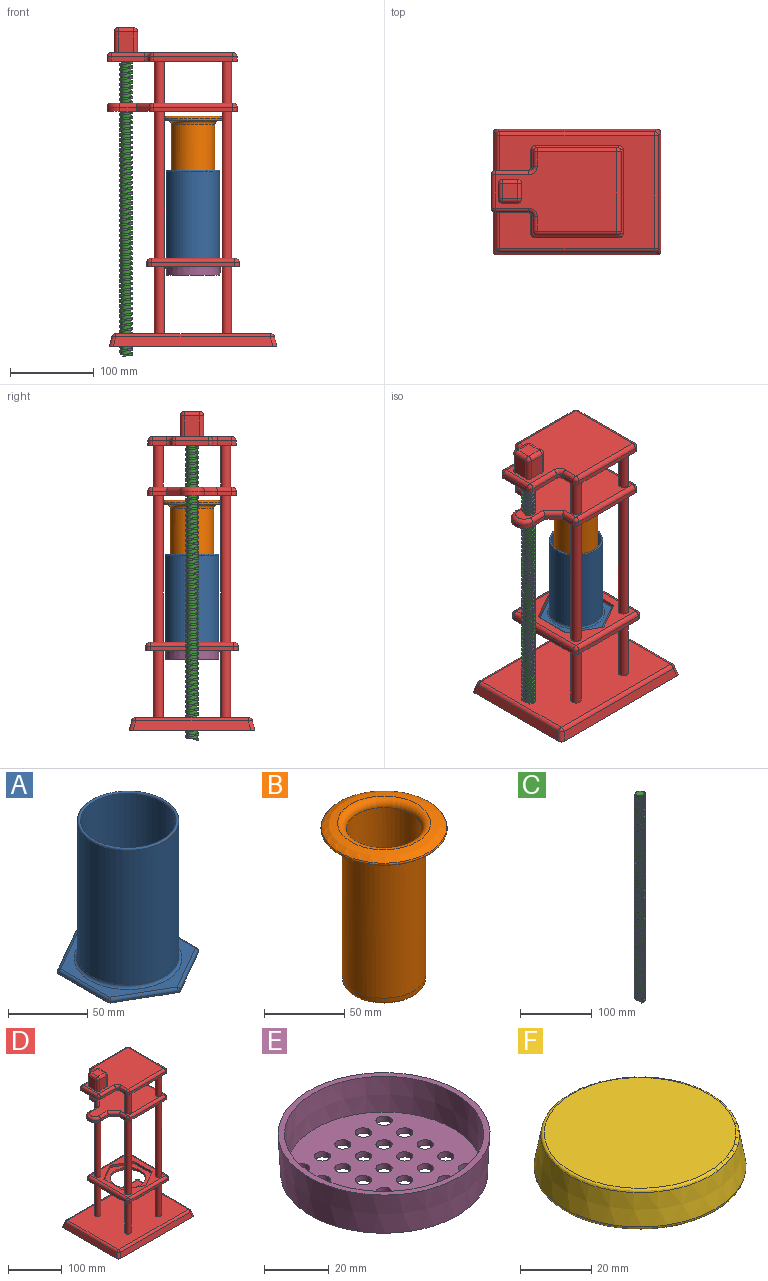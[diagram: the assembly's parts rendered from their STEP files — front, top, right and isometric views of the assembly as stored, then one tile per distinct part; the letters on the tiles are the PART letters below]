
ASSEMBLY  parts=6 mates=5
PART A: 30 faces, bbox 80x91.8x110 mm
  f0: cylinder r=30mm len=109mm, axis (0,0,-1), area 20546mm2, adj f9,f29
  f1: cylinder r=32mm len=104mm, axis (0,0,-1), area 20910.4mm2, adj f10,f29
  f2: plane 87.76x76mm, normal (0,0,1), area 1370.5mm2, adj f10,f14,f15,f20,f21,f25,f26
  f3: plane 43.88x1mm, normal (1,0,0), area 43.9mm2, adj f9,f13,f19,f20
  f4: plane 38x21.94mm, normal (0.5,-0.87,0), area 43.9mm2, adj f9,f11,f13,f14
  f5: plane 38x21.94mm, normal (-0.5,-0.87,0), area 43.9mm2, adj f9,f11,f15,f16
  f6: plane 43.88x1mm, normal (-1,0,0), area 43.9mm2, adj f9,f16,f21,f22
  f7: plane 38x21.94mm, normal (-0.5,0.87,0), area 43.9mm2, adj f9,f22,f26,f28
  f8: plane 38x21.94mm, normal (0.5,0.87,0), area 43.9mm2, adj f9,f19,f25,f28
  f9: plane 91.76x80mm, normal (0,0,-1), area 2713.8mm2, adj f0,f3,f4,f5,f6,f7,f8,f11
  f10: torus R=34mm, axis (0,0,1), area 646mm2, adj f1,f2
  f11: cylinder r=2mm len=2mm, axis (0,0,-1), area 2.1mm2, adj f4,f5,f9,f12
  f12: sphere r=2mm, area 4.2mm2, adj f11,f14,f15
  f13: cylinder r=2mm len=1.73mm, axis (0,0,-1), area 2.1mm2, adj f3,f4,f9,f17
  f14: cylinder r=2mm len=39mm, axis (-0.87,-0.5,0), area 137.8mm2, adj f2,f4,f12,f17
  f15: cylinder r=2mm len=39mm, axis (-0.87,0.5,0), area 137.8mm2, adj f2,f5,f12,f18
  f16: cylinder r=2mm len=1.73mm, axis (0,0,-1), area 2.1mm2, adj f5,f6,f9,f18
  f17: sphere r=2mm, area 4.2mm2, adj f13,f14,f20
  f18: sphere r=2mm, area 4.2mm2, adj f15,f16,f21
  f19: cylinder r=2mm len=1.73mm, axis (0,0,-1), area 2.1mm2, adj f3,f8,f9,f23
  f20: cylinder r=2mm len=43.88mm, axis (0,-1,0), area 137.8mm2, adj f2,f3,f17,f23
  f21: cylinder r=2mm len=43.88mm, axis (0,1,0), area 137.8mm2, adj f2,f6,f18,f24
  f22: cylinder r=2mm len=1.73mm, axis (0,0,-1), area 2.1mm2, adj f6,f7,f9,f24
  f23: sphere r=2mm, area 4.2mm2, adj f19,f20,f25
  f24: sphere r=2mm, area 4.2mm2, adj f21,f22,f26
  f25: cylinder r=2mm len=39mm, axis (0.87,-0.5,0), area 137.8mm2, adj f2,f8,f23,f27
  f26: cylinder r=2mm len=39mm, axis (0.87,0.5,0), area 137.8mm2, adj f2,f7,f24,f27
  f27: sphere r=2mm, area 4.2mm2, adj f25,f26,f28
  f28: cylinder r=2mm len=2mm, axis (0,0,-1), area 2.1mm2, adj f7,f8,f9,f27
  f29: torus R=31mm, axis (0,0,1), area 611.9mm2, adj f0,f1
PART B: 12 faces, bbox 90x90x125 mm
  f0: plane 76.5x76.5mm, normal (0,0,-1), area 1577.8mm2, adj f1,f2
  f1: torus R=38.25mm, axis (0,0,1), area 605.5mm2, adj f0
  f2: torus R=31mm, axis (0,0,1), area 1372.7mm2, adj f0,f3
  f3: cylinder r=26mm len=105mm, axis (0,0,1), area 17153.1mm2, adj f2,f4
  f4: bspline ~52x52mm, area 1356.2mm2, adj f3,f5
  f5: plane 42.01x42.01mm, normal (0,0,-1), area 1385.2mm2, adj f4
  f6: offset ~57x57mm, area 352.7mm2, adj f7,f9
  f7: offset ~54.24x54.24mm, area 333.5mm2, adj f6,f8
  f8: plane 42x42mm, normal (0,0,1), area 1385.2mm2, adj f7
  f9: cylinder r=23.5mm len=109.97mm, axis (0,0,1), area 16237.3mm2, adj f6,f10
  f10: torus R=28.5mm, axis (0,0,-1), area 1315.6mm2, adj f9
  f11: revolved ~77.74x77.74mm, area 4574.4mm2
PART C: 9 faces, bbox 16x18.5x352 mm
  f0: cylinder r=6mm len=350mm, axis (0,0,-1), area 430.2mm2, adj f1,f2,f3,f6,f8
  f1: plane 12x12mm, normal (0,0,1), area 113.1mm2, adj f0
  f2: plane 12x12mm, normal (0,0,-1), area 113.1mm2, adj f0,f5
  f3: plane 2x2mm, normal (0,1,0), area 4mm2, adj f0,f6,f7,f8
  f4: plane 2x1.73mm, normal (-0.87,0.5,0), area 4mm2, adj f5,f6,f7,f8
  f5: cylinder r=6mm len=9mm, axis (0,0,-1), area 12.6mm2, adj f2,f4,f6
  f6: bspline ~350x18.48mm, area 5209.1mm2, adj f0,f3,f4,f5,f7
  f7: cylinder r=8mm len=352mm, axis (0,0,-1), area 5864.3mm2, adj f3,f4,f6,f8
  f8: bspline ~350x18.48mm, area 5209.1mm2, adj f0,f3,f4,f7
PART D: 139 faces, bbox 203.9x150.3x380.5 mm
  f0: cylinder r=6mm len=175mm, axis (0,0,-1), area 6597.3mm2, adj f4,f61
  f1: cylinder r=6mm len=175mm, axis (0,0,-1), area 6597.3mm2, adj f4,f61
  f2: cylinder r=6mm len=175mm, axis (0,0,-1), area 6597.3mm2, adj f4,f61
  f3: cylinder r=6mm len=175mm, axis (0,0,-1), area 6597.3mm2, adj f4,f61
  f4: plane 100x100mm, normal (0,0,1), area 3865.6mm2, adj f0,f1,f2,f3,f35,f36,f40,f41
  f5: cylinder r=6mm len=80mm, axis (0,0,-1), area 3015.9mm2, adj f13,f31
  f6: cylinder r=6mm len=80mm, axis (0,0,-1), area 3015.9mm2, adj f13,f31
  f7: cylinder r=6mm len=80mm, axis (0,0,-1), area 3015.9mm2, adj f13,f31
  f8: cylinder r=6mm len=80mm, axis (0,0,-1), area 3015.9mm2, adj f13,f31
  f9: plane 140.34x11.29mm, normal (0.97,0,0.26), area 1605.6mm2, adj f14,f17,f23,f26
  f10: plane 190.34x11.29mm, normal (0,0.97,0.26), area 2190.2mm2, adj f14,f20,f24,f26
  f11: plane 140.34x11.29mm, normal (-0.97,0,0.26), area 1605.6mm2, adj f14,f15,f19,f20
  f12: plane 190.34x11.29mm, normal (0,-0.97,0.26), area 2190.2mm2, adj f14,f15,f17,f18
  f13: plane 184.29x134.29mm, normal (0,0,1), area 24295.4mm2, adj f5,f6,f7,f8,f18,f19,f23,f24
  f14: plane 200x150mm, normal (0,0,-1), area 29980.4mm2, adj f9,f10,f11,f12,f15,f17,f20,f26
  f15: cylinder r=5mm len=12.25mm, axis (-0.25,-0.25,-0.94), area 93.3mm2, adj f11,f12,f14,f16
  f16: sphere r=5mm, area 26.6mm2, adj f15,f18,f19
  f17: cylinder r=5mm len=12.25mm, axis (0.25,-0.25,-0.94), area 93.3mm2, adj f9,f12,f14,f21
  f18: cylinder r=5mm len=184.29mm, axis (-1,0,0), area 1206.2mm2, adj f12,f13,f16,f21
  f19: cylinder r=5mm len=134.29mm, axis (0,-1,0), area 878.9mm2, adj f11,f13,f16,f22
  f20: cylinder r=5mm len=12.25mm, axis (-0.25,0.25,-0.94), area 93.3mm2, adj f10,f11,f14,f22
  f21: sphere r=5mm, area 26.6mm2, adj f17,f18,f23
  f22: sphere r=5mm, area 26.6mm2, adj f19,f20,f24
  f23: cylinder r=5mm len=134.29mm, axis (0,-1,0), area 878.9mm2, adj f9,f13,f21,f25
  f24: cylinder r=5mm len=184.29mm, axis (-1,0,0), area 1206.2mm2, adj f10,f13,f22,f25
  f25: sphere r=5mm, area 26.6mm2, adj f23,f24,f26
  f26: cylinder r=5mm len=12.25mm, axis (0.25,0.25,-0.94), area 93.3mm2, adj f9,f10,f14,f25
  f27: plane 100x5mm, normal (1,0,0), area 500mm2, adj f31,f34,f40,f43
  f28: plane 100x5mm, normal (0,1,0), area 500mm2, adj f31,f37,f41,f43
  f29: plane 100x5mm, normal (-1,0,0), area 500mm2, adj f31,f32,f36,f37
  f30: plane 100x5mm, normal (0,-1,0), area 500mm2, adj f31,f32,f34,f35
  f31: plane 110x110mm, normal (0,0,-1), area 8205mm2, adj f5,f6,f7,f8,f27,f28,f29,f30
  f32: cylinder r=5mm len=5mm, axis (0,0,1), area 39.3mm2, adj f29,f30,f31,f33
  f33: sphere r=5mm, area 39.3mm2, adj f32,f35,f36
  f34: cylinder r=5mm len=5mm, axis (0,0,-1), area 39.3mm2, adj f27,f30,f31,f38
  f35: cylinder r=5mm len=100mm, axis (-1,0,0), area 785.4mm2, adj f4,f30,f33,f38
  f36: cylinder r=5mm len=100mm, axis (0,1,0), area 785.4mm2, adj f4,f29,f33,f39
  f37: cylinder r=5mm len=5mm, axis (0,0,-1), area 39.3mm2, adj f28,f29,f31,f39
  f38: sphere r=5mm, area 39.3mm2, adj f34,f35,f40
  f39: sphere r=5mm, area 39.3mm2, adj f36,f37,f41
  f40: cylinder r=5mm len=100mm, axis (0,-1,0), area 785.4mm2, adj f4,f27,f38,f42
  f41: cylinder r=5mm len=100mm, axis (1,0,0), area 785.4mm2, adj f4,f28,f39,f42
  f42: sphere r=5mm, area 39.3mm2, adj f40,f41,f43
  f43: cylinder r=5mm len=5mm, axis (0,0,1), area 39.3mm2, adj f27,f28,f31,f42
  f44: plane 40.5x23.38mm, normal (-0.5,0.87,0), area 233.8mm2, adj f4,f45,f49,f50
  f45: plane 46.77x5mm, normal (-1,0,0), area 233.8mm2, adj f4,f44,f46,f50
  f46: plane 40.5x23.38mm, normal (-0.5,-0.87,0), area 233.8mm2, adj f4,f45,f47,f50
  f47: plane 40.5x23.38mm, normal (0.5,-0.87,0), area 233.8mm2, adj f4,f46,f48,f50
  f48: plane 46.77x5mm, normal (1,0,0), area 233.8mm2, adj f4,f47,f49,f50
  f49: plane 40.5x23.38mm, normal (0.5,0.87,0), area 233.8mm2, adj f4,f44,f48,f50
  f50: plane 93.53x81mm, normal (0,0,1), area 2260.8mm2, adj f44,f45,f46,f47,f48,f49,f51
  f51: cylinder r=33mm len=66mm, axis (0,0,1), area 1036.7mm2, adj f31,f50
  f52: plane 17.5x5mm, normal (-1,0,0), area 87.5mm2, adj f61,f66,f82,f88
  f53: plane 20x5mm, normal (0,1,0), area 100mm2, adj f54,f61,f66,f92
  f54: cylinder r=15mm len=30mm, axis (0,0,-1), area 235.6mm2, adj f53,f55,f61,f94
  f55: plane 20x5mm, normal (0,-1,0), area 100mm2, adj f54,f61,f67,f95
  f56: plane 17.5x5mm, normal (-1,0,0), area 87.5mm2, adj f61,f67,f87,f91
  f57: plane 95x5mm, normal (0,-1,0), area 475mm2, adj f61,f81,f86,f87
  f58: plane 95x5mm, normal (1,0,0), area 475mm2, adj f61,f78,f80,f81
  f59: plane 95x5mm, normal (0,1,0), area 475mm2, adj f61,f78,f82,f83
  f60: plane 145x95mm, normal (0,0,1), area 9851.1mm2, adj f62,f63,f64,f65,f80,f83,f86,f88
  f61: plane 155x105mm, normal (0,0,-1), area 12179.6mm2, adj f0,f1,f2,f3,f52,f53,f54,f55
  f62: cylinder r=6mm len=50mm, axis (0,0,-1), area 1885mm2, adj f60,f77
  f63: cylinder r=6mm len=50mm, axis (0,0,-1), area 1885mm2, adj f60,f77
  f64: cylinder r=6mm len=50mm, axis (0,0,-1), area 1885mm2, adj f60,f77
  f65: cylinder r=6mm len=50mm, axis (0,0,-1), area 1885mm2, adj f60,f77
  f66: plane 15x15mm, normal (-0.71,0.71,0), area 106.1mm2, adj f52,f53,f61,f90
  f67: plane 15x15mm, normal (-0.71,-0.71,0), area 106.1mm2, adj f55,f56,f61,f93
  f68: plane 17.5x5mm, normal (-1,0,0), area 87.5mm2, adj f77,f96,f98,f99
  f69: plane 40x5mm, normal (0,1,0), area 200mm2, adj f77,f98,f104,f105
  f70: plane 40x5mm, normal (-1,0,0), area 200mm2, adj f77,f104,f110,f111
  f71: plane 40x5mm, normal (0,-1,0), area 200mm2, adj f77,f110,f116,f119
  f72: plane 17.5x5mm, normal (-1,0,0), area 87.5mm2, adj f77,f113,f117,f119
  f73: plane 95x5mm, normal (0,-1,0), area 475mm2, adj f77,f107,f112,f113
  f74: plane 95x5mm, normal (1,0,0), area 475mm2, adj f77,f101,f106,f107
  f75: plane 95x5mm, normal (0,1,0), area 475mm2, adj f77,f96,f100,f101
  f76: plane 145x95mm, normal (0,0,1), area 10305.4mm2, adj f99,f100,f102,f105,f106,f111,f112,f116
  f77: plane 155x105mm, normal (0,0,-1), area 12874.4mm2, adj f62,f63,f64,f65,f68,f69,f70,f71
  f78: cylinder r=5mm len=5mm, axis (0,0,1), area 39.3mm2, adj f58,f59,f61,f79
  f79: sphere r=5mm, area 39.3mm2, adj f78,f80,f83
  f80: cylinder r=5mm len=95mm, axis (0,-1,0), area 746.1mm2, adj f58,f60,f79,f84
  f81: cylinder r=5mm len=5mm, axis (0,0,-1), area 39.3mm2, adj f57,f58,f61,f84
  f82: cylinder r=5mm len=5mm, axis (0,0,-1), area 39.3mm2, adj f52,f59,f61,f85
  f83: cylinder r=5mm len=95mm, axis (1,0,0), area 746.1mm2, adj f59,f60,f79,f85
  f84: sphere r=5mm, area 39.3mm2, adj f80,f81,f86
  f85: sphere r=5mm, area 39.3mm2, adj f82,f83,f88
  f86: cylinder r=5mm len=95mm, axis (-1,0,0), area 746.1mm2, adj f57,f60,f84,f89
  f87: cylinder r=5mm len=5mm, axis (0,0,1), area 39.3mm2, adj f56,f57,f61,f89
  f88: cylinder r=5mm len=19.57mm, axis (0,1,0), area 143.4mm2, adj f52,f60,f85,f90
  f89: sphere r=5mm, area 39.3mm2, adj f86,f87,f91
  f90: cylinder r=5mm len=21.46mm, axis (-0.71,-0.71,0), area 178.4mm2, adj f60,f66,f88,f92
  f91: cylinder r=5mm len=19.57mm, axis (0,1,0), area 143.4mm2, adj f56,f60,f89,f93
  f92: cylinder r=5mm len=22.07mm, axis (1,0,0), area 163mm2, adj f53,f60,f90,f94
  f93: cylinder r=5mm len=21.46mm, axis (-0.71,0.71,0), area 178.4mm2, adj f60,f67,f91,f95
  f94: torus R=10mm, axis (0,0,1), area 325.3mm2, adj f54,f60,f92,f95
  f95: cylinder r=5mm len=22.07mm, axis (-1,0,0), area 163mm2, adj f55,f60,f93,f94
  f96: cylinder r=5mm len=5mm, axis (0,0,-1), area 39.3mm2, adj f68,f75,f77,f97
  f97: sphere r=5mm, area 39.3mm2, adj f96,f99,f100
  f98: cylinder r=5mm len=5mm, axis (0,0,1), area 39.3mm2, adj f68,f69,f77,f102
  f99: cylinder r=5mm len=17.5mm, axis (0,1,0), area 137.4mm2, adj f68,f76,f97,f102
  f100: cylinder r=5mm len=95mm, axis (1,0,0), area 746.1mm2, adj f75,f76,f97,f103
  f101: cylinder r=5mm len=5mm, axis (0,0,1), area 39.3mm2, adj f74,f75,f77,f103
  f102: torus R=10mm, axis (0,0,1), area 84.1mm2, adj f76,f98,f99,f105
  f103: sphere r=5mm, area 39.3mm2, adj f100,f101,f106
  f104: cylinder r=5mm len=5mm, axis (0,0,-1), area 39.3mm2, adj f69,f70,f77,f108
  f105: cylinder r=5mm len=40mm, axis (1,0,0), area 314.2mm2, adj f69,f76,f102,f108
  f106: cylinder r=5mm len=95mm, axis (0,-1,0), area 746.1mm2, adj f74,f76,f103,f109
  f107: cylinder r=5mm len=5mm, axis (0,0,-1), area 39.3mm2, adj f73,f74,f77,f109
  f108: sphere r=5mm, area 39.3mm2, adj f104,f105,f111
  f109: sphere r=5mm, area 39.3mm2, adj f106,f107,f112
  f110: cylinder r=5mm len=5mm, axis (0,0,1), area 39.3mm2, adj f70,f71,f77,f114
  f111: cylinder r=5mm len=40mm, axis (0,1,0), area 314.2mm2, adj f70,f76,f108,f114
  f112: cylinder r=5mm len=95mm, axis (-1,0,0), area 746.1mm2, adj f73,f76,f109,f115
  f113: cylinder r=5mm len=5mm, axis (0,0,1), area 39.3mm2, adj f72,f73,f77,f115
  f114: sphere r=5mm, area 39.3mm2, adj f110,f111,f116
  f115: sphere r=5mm, area 39.3mm2, adj f112,f113,f117
  f116: cylinder r=5mm len=40mm, axis (-1,0,0), area 314.2mm2, adj f71,f76,f114,f118
  f117: cylinder r=5mm len=17.5mm, axis (0,1,0), area 137.4mm2, adj f72,f76,f115,f118
  f118: torus R=10mm, axis (0,0,1), area 84.1mm2, adj f76,f116,f117,f119
  f119: cylinder r=5mm len=5mm, axis (0,0,-1), area 39.3mm2, adj f71,f72,f77,f118
  f120: cylinder r=7.5mm len=35mm, axis (0,0,1), area 1649.3mm2, adj f77,f125
  f121: plane 25x18mm, normal (1,0,0), area 450mm2, adj f76,f127,f128,f129
  f122: plane 25x18mm, normal (0,1,0), area 450mm2, adj f76,f127,f132,f133
  f123: plane 25x18mm, normal (-1,0,0), area 450mm2, adj f76,f132,f135,f138
  f124: plane 25x18mm, normal (0,-1,0), area 450mm2, adj f76,f129,f134,f135
  f125: plane 15x15mm, normal (0,0,-1), area 176.7mm2, adj f120
  f126: plane 18x18mm, normal (0,0,1), area 324mm2, adj f128,f133,f134,f138
  f127: cylinder r=5mm len=25mm, axis (0,0,1), area 196.3mm2, adj f76,f121,f122,f130
  f128: cylinder r=5mm len=18mm, axis (0,-1,0), area 141.4mm2, adj f121,f126,f130,f131
  f129: cylinder r=5mm len=25mm, axis (0,0,-1), area 196.3mm2, adj f76,f121,f124,f131
  f130: sphere r=5mm, area 39.3mm2, adj f127,f128,f133
  f131: sphere r=5mm, area 39.3mm2, adj f128,f129,f134
  f132: cylinder r=5mm len=25mm, axis (0,0,-1), area 196.3mm2, adj f76,f122,f123,f136
  f133: cylinder r=5mm len=18mm, axis (1,0,0), area 141.4mm2, adj f122,f126,f130,f136
  f134: cylinder r=5mm len=18mm, axis (-1,0,0), area 141.4mm2, adj f124,f126,f131,f137
  f135: cylinder r=5mm len=25mm, axis (0,0,1), area 196.3mm2, adj f76,f123,f124,f137
  f136: sphere r=5mm, area 39.3mm2, adj f132,f133,f138
  f137: sphere r=5mm, area 39.3mm2, adj f134,f135,f138
  f138: cylinder r=5mm len=18mm, axis (0,1,0), area 141.4mm2, adj f123,f126,f136,f137
PART E: 30 faces, bbox 65.6x65.6x15 mm
  f0: cone r=32mm half-angle=3deg, axis (0,0,1), area 3057.2mm2, adj f1,f2
  f1: plane 65.57x65.57mm, normal (0,0,1), area 400mm2, adj f0,f3
  f2: plane 64x64mm, normal (0,0,-1), area 2726.1mm2, adj f0,f5,f6,f7,f8,f9,f10,f11
  f3: cone r=30mm half-angle=3deg, axis (0,0,1), area 2490mm2, adj f1,f4
  f4: plane 60.2x60.2mm, normal (0,0,1), area 2355.8mm2, adj f3,f5,f6,f7,f8,f9,f10,f11
  f5: cylinder r=2.5mm len=5mm, axis (0,0,1), area 31.4mm2, adj f2,f4
  f6: cylinder r=2.5mm len=5mm, axis (0,0,1), area 31.4mm2, adj f2,f4
  f7: cylinder r=2.5mm len=5mm, axis (0,0,1), area 31.4mm2, adj f2,f4
  f8: cylinder r=2.5mm len=5mm, axis (0,0,1), area 31.4mm2, adj f2,f4
  f9: cylinder r=2.5mm len=5mm, axis (0,0,1), area 31.4mm2, adj f2,f4
  f10: cylinder r=2.5mm len=5mm, axis (0,0,1), area 31.4mm2, adj f2,f4
  f11: cylinder r=2.5mm len=5mm, axis (0,0,1), area 31.4mm2, adj f2,f4
  f12: cylinder r=2.5mm len=5mm, axis (0,0,1), area 31.4mm2, adj f2,f4
  f13: cylinder r=2.5mm len=5mm, axis (0,0,1), area 31.4mm2, adj f2,f4
  f14: cylinder r=2.5mm len=5mm, axis (0,0,1), area 31.4mm2, adj f2,f4
  f15: cylinder r=2.5mm len=5mm, axis (0,0,1), area 31.4mm2, adj f2,f4
  f16: cylinder r=2.5mm len=5mm, axis (0,0,1), area 31.4mm2, adj f2,f4
  f17: cylinder r=2.5mm len=5mm, axis (0,0,1), area 31.4mm2, adj f2,f4
  f18: cylinder r=2.5mm len=5mm, axis (0,0,1), area 31.4mm2, adj f2,f4
  f19: cylinder r=2.5mm len=5mm, axis (0,0,1), area 31.4mm2, adj f2,f4
  f20: cylinder r=2.5mm len=5mm, axis (0,0,1), area 31.4mm2, adj f2,f4
  f21: cylinder r=2.5mm len=5mm, axis (0,0,1), area 31.4mm2, adj f2,f4
  f22: cylinder r=2.5mm len=5mm, axis (0,0,1), area 31.4mm2, adj f2,f4
  f23: cylinder r=2.5mm len=5mm, axis (0,0,1), area 31.4mm2, adj f2,f4
  f24: cylinder r=2.5mm len=5mm, axis (0,0,1), area 31.4mm2, adj f2,f4
  f25: cylinder r=2.5mm len=5mm, axis (0,0,1), area 31.4mm2, adj f2,f4
  f26: cylinder r=2.5mm len=5mm, axis (0,0,1), area 31.4mm2, adj f2,f4
  f27: cylinder r=2.5mm len=5mm, axis (0,0,1), area 31.4mm2, adj f2,f4
  f28: cylinder r=2.5mm len=5mm, axis (0,0,1), area 31.4mm2, adj f2,f4
  f29: cylinder r=2.5mm len=5mm, axis (0,0,1), area 31.4mm2, adj f2,f4
PART F: 5 faces, bbox 64.5x64.5x12.5 mm
  f0: cone r=30mm half-angle=10deg, axis (0,0,-1), area 1933.9mm2, adj f3,f4
  f1: plane 53.91x53.91mm, normal (0,0,1), area 2282.9mm2, adj f4
  f2: plane 57.62x57.62mm, normal (0,0,-1), area 2607.3mm2, adj f3
  f3: torus R=28.81mm, axis (0,0,1), area 323.3mm2, adj f0,f2
  f4: torus R=26.96mm, axis (0,0,1), area 241.7mm2, adj f0,f1
PLACE A t=(-33.13,17.07,-5.2)mm
PLACE B t=(-33.13,17.07,49.3)mm
PLACE C t=(-113.13,17.07,-115.2)mm
PLACE D t=(-33.13,17.07,-105.2)mm
PLACE E t=(-33.13,17.07,-20.2)mm
PLACE F t=(-33.13,17.07,36.8)mm
MATE fastened E.f0 <-> A.f0  axis (0,0,1) through (-33.13,17.07,-5.2)mm
MATE fastened C.f0 <-> D.f120  axis (0,0,1) through (-113.13,17.07,234.8)mm
MATE fastened B.f1 <-> F.f0  axis (0,0,-1) through (-33.13,17.07,49.3)mm
MATE fastened E.f0 <-> D.f51  axis (0,0,1) through (-33.13,17.07,-5.2)mm
MATE fastened F.f0 <-> A.f0  axis (0,0,1) through (-33.13,17.07,49.3)mm
